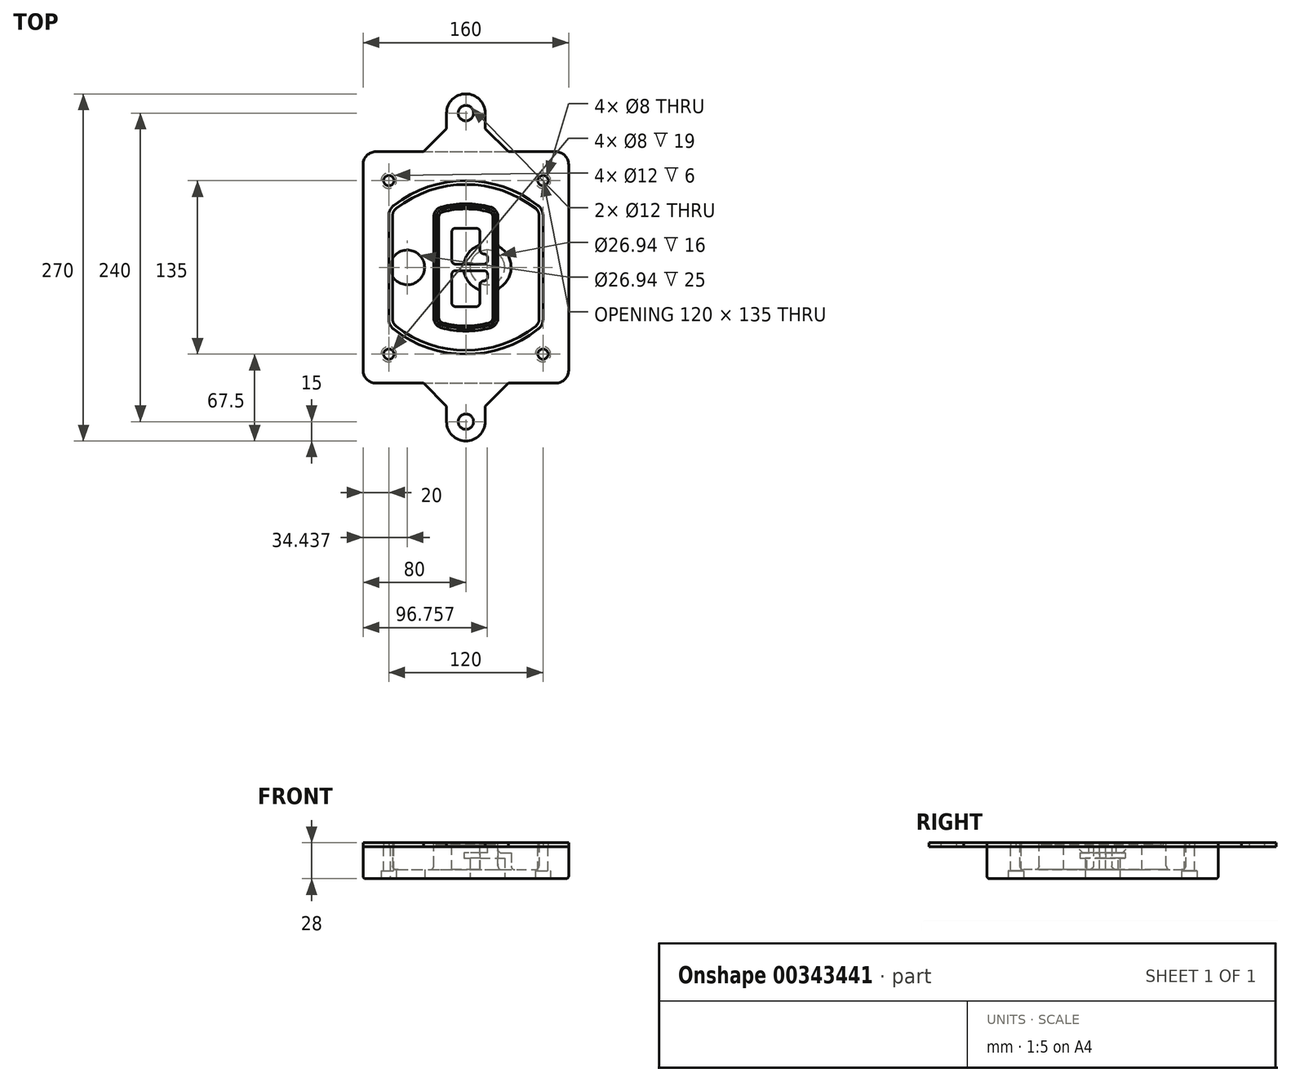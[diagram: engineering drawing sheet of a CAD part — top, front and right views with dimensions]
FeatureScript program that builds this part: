
annotation { "Feature Type Name" : "Feature", "Feature Type Description" : "" }
export const myFeature = defineFeature(function(context is Context, id is Id, definition is map)
    precondition{}
    {
        {
            var Q0;
            Q0=qCreatedBy(makeId("Top.planeOp"),FACE);
            var sketch = newSketch(context, id + "F0", { "sketchPlane" : qUnion([Q0])});
            skPoint(sketch, "E0.rect.middle", {"position": v(0, 0) * mm});
            skLineSegment(sketch, "E1.bottom", {"start": v(-70, -90) * mm, "end": v(70, -90) * mm});
            skLineSegment(sketch, "E1.top", {"start": v(-70, 90) * mm, "end": v(70, 90) * mm});
            skLineSegment(sketch, "E1.left", {"start": v(-80, -80) * mm, "end": v(-80, 80) * mm});
            skLineSegment(sketch, "E1.right", {"start": v(80, -80) * mm, "end": v(80, 80) * mm});
            skLineSegment(sketch, "E2", {"start": v(-80, 90) * mm, "end": v(80, -90) * mm, "construction": true});
            skLineSegment(sketch, "E3", {"start": v(80, 90) * mm, "end": v(-80, -90) * mm, "construction": true});
            skCircle(sketch, "E4", {"center": v(-60, 67.5) * mm, "radius": 4 * mm});
            skCircle(sketch, "E5", {"center": v(60, 67.5) * mm, "radius": 4 * mm});
            skCircle(sketch, "E6", {"center": v(60, -67.5) * mm, "radius": 4 * mm});
            skCircle(sketch, "E7", {"center": v(-60, -67.5) * mm, "radius": 4 * mm});
            skLineSegment(sketch, "E8", {"start": v(-60, 67.5) * mm, "end": v(60, 67.5) * mm, "construction": true});
            skLineSegment(sketch, "E9", {"start": v(60, 67.5) * mm, "end": v(60, -67.5) * mm, "construction": true});
            skLineSegment(sketch, "E10", {"start": v(60, -67.5) * mm, "end": v(-60, -67.5) * mm, "construction": true});
            skLineSegment(sketch, "E11", {"start": v(-60, -67.5) * mm, "end": v(-60, 67.5) * mm, "construction": true});
            skLineSegment(sketch, "E12", {"start": v(-60, 40.3) * mm, "end": v(-60, -40.3) * mm});
            skLineSegment(sketch, "E13", {"start": v(60, 40.3) * mm, "end": v(60, -40.3) * mm});
            skArc(sketch, "E14", {"start": v(56.15, 48.18) * mm, "mid": v(0, 67.5) * mm, "end": v(-56.15, 48.18) * mm});
            skArc(sketch, "E15", {"start": v(-56.15, -48.18) * mm, "mid": v(0, -67.5) * mm, "end": v(56.15, -48.18) * mm});
            skLineSegment(sketch, "E16", {"start": v(-60, 0) * mm, "end": v(60, 0) * mm, "construction": true});
            skPoint(sketch, "E17.visualSharp", {"position": v(-60, -45) * mm});
            skArc(sketch, "E17.filletArc", {"start": v(-60, -40.3) * mm, "mid": v(-58.99, -44.68) * mm, "end": v(-56.15, -48.18) * mm});
            skPoint(sketch, "E18.visualSharp", {"position": v(-60, 45) * mm});
            skArc(sketch, "E18.filletArc", {"start": v(-56.15, 48.18) * mm, "mid": v(-58.99, 44.68) * mm, "end": v(-60, 40.3) * mm});
            skPoint(sketch, "E19.visualSharp", {"position": v(60, 45) * mm});
            skArc(sketch, "E19.filletArc", {"start": v(60, 40.3) * mm, "mid": v(58.99, 44.68) * mm, "end": v(56.15, 48.18) * mm});
            skPoint(sketch, "E20.visualSharp", {"position": v(60, -45) * mm});
            skArc(sketch, "E20.filletArc", {"start": v(56.15, -48.18) * mm, "mid": v(58.99, -44.68) * mm, "end": v(60, -40.3) * mm});
            skPoint(sketch, "E21.visualSharp", {"position": v(-80, 90) * mm});
            skArc(sketch, "E21.filletArc", {"start": v(-70, 90) * mm, "mid": v(-77.07, 87.07) * mm, "end": v(-80, 80) * mm});
            skPoint(sketch, "E22.visualSharp", {"position": v(80, 90) * mm});
            skArc(sketch, "E22.filletArc", {"start": v(80, 80) * mm, "mid": v(77.07, 87.07) * mm, "end": v(70, 90) * mm});
            skPoint(sketch, "E23.visualSharp", {"position": v(80, -90) * mm});
            skArc(sketch, "E23.filletArc", {"start": v(70, -90) * mm, "mid": v(77.07, -87.07) * mm, "end": v(80, -80) * mm});
            skPoint(sketch, "E24.visualSharp", {"position": v(-80, -90) * mm});
            skArc(sketch, "E24.filletArc", {"start": v(-80, -80) * mm, "mid": v(-77.07, -87.07) * mm, "end": v(-70, -90) * mm});
            skArc(sketch, "E25.0", {"start": v(57, 40.3) * mm, "mid": v(56.3, 43.36) * mm, "end": v(54.3, 45.81) * mm});
            skLineSegment(sketch, "E25.1", {"start": v(57, 40.3) * mm, "end": v(57, -40.3) * mm});
            skArc(sketch, "E25.2", {"start": v(54.3, -45.81) * mm, "mid": v(56.3, -43.36) * mm, "end": v(57, -40.3) * mm});
            skArc(sketch, "E25.3", {"start": v(-54.3, -45.81) * mm, "mid": v(0, -64.5) * mm, "end": v(54.3, -45.81) * mm});
            skArc(sketch, "E25.4", {"start": v(-57, -40.3) * mm, "mid": v(-56.3, -43.36) * mm, "end": v(-54.3, -45.81) * mm});
            skArc(sketch, "E25.5", {"start": v(54.3, 45.81) * mm, "mid": v(0, 64.5) * mm, "end": v(-54.3, 45.81) * mm});
            skLineSegment(sketch, "E25.6", {"start": v(-57, 40.3) * mm, "end": v(-57, -40.3) * mm});
            skArc(sketch, "E25.7", {"start": v(-54.3, 45.81) * mm, "mid": v(-56.3, 43.36) * mm, "end": v(-57, 40.3) * mm});
            skArc(sketch, "E26.0", {"start": v(-58.62, 51.33) * mm, "mid": v(-62.58, 46.43) * mm, "end": v(-64, 40.3) * mm});
            skArc(sketch, "E26.1", {"start": v(58.62, 51.33) * mm, "mid": v(0, 71.5) * mm, "end": v(-58.62, 51.33) * mm});
            skArc(sketch, "E26.2", {"start": v(64, 40.3) * mm, "mid": v(62.58, 46.43) * mm, "end": v(58.62, 51.33) * mm});
            skLineSegment(sketch, "E26.3", {"start": v(64, 40.3) * mm, "end": v(64, -40.3) * mm});
            skArc(sketch, "E26.4", {"start": v(58.62, -51.33) * mm, "mid": v(62.58, -46.43) * mm, "end": v(64, -40.3) * mm});
            skLineSegment(sketch, "E26.5", {"start": v(-64, 40.3) * mm, "end": v(-64, -40.3) * mm});
            skArc(sketch, "E26.6", {"start": v(-58.62, -51.33) * mm, "mid": v(0, -71.5) * mm, "end": v(58.62, -51.33) * mm});
            skArc(sketch, "E26.7", {"start": v(-64, -40.3) * mm, "mid": v(-62.58, -46.43) * mm, "end": v(-58.62, -51.33) * mm});
            skSolve(sketch);
        }
        {
            var Q0;
            Q0=makeQuery(id+"F0.imprint","IMPRINT",FACE,{"disambiguationData":[TD([[makeQuery(id+"F0.imprint","IMPRINT",EDGE,{"derivedFrom":sQuery(id+"F0.wireOp",EDGE,"E1.bottom")}),1.0]])]});
            var Q1;
            Q1=makeQuery(id+"F0.imprint","IMPRINT",FACE,{"disambiguationData":[TD([[makeQuery(id+"F0.imprint","IMPRINT",EDGE,{"derivedFrom":sQuery(id+"F0.wireOp",EDGE,"E12")}),1.0]])]});
            var Q2;
            Q2=makeQuery(id+"F0.imprint","IMPRINT",FACE,{"disambiguationData":[TD([[makeQuery(id+"F0.imprint","IMPRINT",EDGE,{"derivedFrom":sQuery(id+"F0.wireOp",EDGE,"E25.0")}),1.0]])]});
            var Q3;
            Q3=makeQuery(id+"F0.imprint","IMPRINT",FACE,{"disambiguationData":[TD([[makeQuery(id+"F0.imprint","IMPRINT",EDGE,{"derivedFrom":sQuery(id+"F0.wireOp",EDGE,"E12")}),-1.0]])]});
            extrude(context, id + "F1", {"entities" : qUnion([Q0, Q1, Q2, Q3]), "oppositeDirection" : true, "depth" : 25 * mm});
        }
        {
            var Q0;
            Q0=makeQuery(id+"F0.imprint","IMPRINT",FACE,{"disambiguationData":[TD([[makeQuery(id+"F0.imprint","IMPRINT",EDGE,{"derivedFrom":sQuery(id+"F0.wireOp",EDGE,"E12")}),1.0]])]});
            extrude(context, id + "F2", {"entities" : qUnion([Q0]), "operationType" : NewBodyOperationType.ADD, "depth" : 3 * mm});
        }
        {
            var Q0;
            Q0=makeQuery(id+"F0.imprint","IMPRINT",FACE,{"disambiguationData":[TD([[makeQuery(id+"F0.imprint","IMPRINT",EDGE,{"derivedFrom":sQuery(id+"F0.wireOp",EDGE,"E25.0")}),1.0]])]});
            extrude(context, id + "F3", {"entities" : qUnion([Q0]), "operationType" : NewBodyOperationType.REMOVE, "oppositeDirection" : true, "depth" : 18 * mm});
        }
        {
            var Q0;
            Q0=makeQuery(id+"F2.opExtrude","CAP_FACE",FACE,{"disambiguationData":[OSD([sQuery(id+"F0.wireOp",EDGE,"E12"),sQuery(id+"F0.wireOp",EDGE,"E13"),sQuery(id+"F0.wireOp",EDGE,"E14"),sQuery(id+"F0.wireOp",EDGE,"E15"),sQuery(id+"F0.wireOp",EDGE,"E17.filletArc"),sQuery(id+"F0.wireOp",EDGE,"E18.filletArc"),sQuery(id+"F0.wireOp",EDGE,"E19.filletArc"),sQuery(id+"F0.wireOp",EDGE,"E20.filletArc"),sQuery(id+"F0.wireOp",EDGE,"E25.0"),sQuery(id+"F0.wireOp",EDGE,"E25.1"),sQuery(id+"F0.wireOp",EDGE,"E25.2"),sQuery(id+"F0.wireOp",EDGE,"E25.3"),sQuery(id+"F0.wireOp",EDGE,"E25.4"),sQuery(id+"F0.wireOp",EDGE,"E25.5"),sQuery(id+"F0.wireOp",EDGE,"E25.6"),sQuery(id+"F0.wireOp",EDGE,"E25.7")])],"isStart":false});
            var sketch = newSketch(context, id + "F4", { "sketchPlane" : qUnion([Q0])});
            skArc(sketch, "E27.0", {"start": v(-19.08, -46.97) * mm, "mid": v(0, -49.5) * mm, "end": v(19.08, -46.97) * mm});
            skArc(sketch, "E28.0", {"start": v(19.08, 46.97) * mm, "mid": v(0, 49.5) * mm, "end": v(-19.08, 46.97) * mm});
            skLineSegment(sketch, "E29", {"start": v(-25, 39.25) * mm, "end": v(-25, -39.25) * mm});
            skLineSegment(sketch, "E30", {"start": v(25, 39.25) * mm, "end": v(25, -39.25) * mm});
            skLineSegment(sketch, "E31", {"start": v(-25, 45.1) * mm, "end": v(25, 45.1) * mm, "construction": true});
            skLineSegment(sketch, "E32", {"start": v(-25, -45.1) * mm, "end": v(25, -45.1) * mm, "construction": true});
            skPoint(sketch, "E33.visualSharp", {"position": v(-25, 45.1) * mm});
            skArc(sketch, "E33.filletArc", {"start": v(-19.08, 46.97) * mm, "mid": v(-23.35, 44.11) * mm, "end": v(-25, 39.25) * mm});
            skPoint(sketch, "E34.visualSharp", {"position": v(25, 45.1) * mm});
            skArc(sketch, "E34.filletArc", {"start": v(25, 39.25) * mm, "mid": v(23.35, 44.11) * mm, "end": v(19.08, 46.97) * mm});
            skPoint(sketch, "E35.visualSharp", {"position": v(25, -45.1) * mm});
            skArc(sketch, "E35.filletArc", {"start": v(19.08, -46.97) * mm, "mid": v(23.35, -44.11) * mm, "end": v(25, -39.25) * mm});
            skPoint(sketch, "E36.visualSharp", {"position": v(-25, -45.1) * mm});
            skArc(sketch, "E36.filletArc", {"start": v(-25, -39.25) * mm, "mid": v(-23.35, -44.11) * mm, "end": v(-19.08, -46.97) * mm});
            skArc(sketch, "E37.0", {"start": v(54.3, 45.81) * mm, "mid": v(0, 64.5) * mm, "end": v(-54.3, 45.81) * mm});
            skArc(sketch, "E37.1", {"start": v(-54.3, 45.81) * mm, "mid": v(-56.3, 43.36) * mm, "end": v(-57, 40.3) * mm});
            skLineSegment(sketch, "E37.2", {"start": v(-57, 40.3) * mm, "end": v(-57, -40.3) * mm});
            skArc(sketch, "E37.3", {"start": v(-57, -40.3) * mm, "mid": v(-56.3, -43.36) * mm, "end": v(-54.3, -45.81) * mm});
            skArc(sketch, "E37.4", {"start": v(-54.3, -45.81) * mm, "mid": v(0, -64.5) * mm, "end": v(54.3, -45.81) * mm});
            skArc(sketch, "E37.5", {"start": v(54.3, -45.81) * mm, "mid": v(56.3, -43.36) * mm, "end": v(57, -40.3) * mm});
            skLineSegment(sketch, "E37.6", {"start": v(57, 40.3) * mm, "end": v(57, -40.3) * mm});
            skArc(sketch, "E37.7", {"start": v(57, 40.3) * mm, "mid": v(56.3, 43.36) * mm, "end": v(54.3, 45.81) * mm});
            skLineSegment(sketch, "E38.0", {"start": v(23, 39.25) * mm, "end": v(23, -39.25) * mm});
            skArc(sketch, "E38.1", {"start": v(18.56, -45.04) * mm, "mid": v(21.76, -42.9) * mm, "end": v(23, -39.25) * mm});
            skArc(sketch, "E38.2", {"start": v(-18.56, -45.04) * mm, "mid": v(0, -47.5) * mm, "end": v(18.56, -45.04) * mm});
            skArc(sketch, "E38.3", {"start": v(-23, -39.25) * mm, "mid": v(-21.76, -42.9) * mm, "end": v(-18.56, -45.04) * mm});
            skLineSegment(sketch, "E38.4", {"start": v(-23, 39.25) * mm, "end": v(-23, -39.25) * mm});
            skArc(sketch, "E38.5", {"start": v(23, 39.25) * mm, "mid": v(21.76, 42.9) * mm, "end": v(18.56, 45.04) * mm});
            skArc(sketch, "E38.6", {"start": v(-18.56, 45.04) * mm, "mid": v(-21.76, 42.9) * mm, "end": v(-23, 39.25) * mm});
            skArc(sketch, "E38.7", {"start": v(18.56, 45.04) * mm, "mid": v(0, 47.5) * mm, "end": v(-18.56, 45.04) * mm});
            skArc(sketch, "E39.0", {"start": v(21, 39.25) * mm, "mid": v(20.18, 41.68) * mm, "end": v(18.04, 43.1) * mm});
            skLineSegment(sketch, "E39.1", {"start": v(21, 39.25) * mm, "end": v(21, -39.25) * mm});
            skArc(sketch, "E39.2", {"start": v(18.04, -43.1) * mm, "mid": v(20.18, -41.68) * mm, "end": v(21, -39.25) * mm});
            skArc(sketch, "E39.3", {"start": v(-18.04, -43.1) * mm, "mid": v(0, -45.5) * mm, "end": v(18.04, -43.1) * mm});
            skArc(sketch, "E39.4", {"start": v(-21, -39.25) * mm, "mid": v(-20.18, -41.68) * mm, "end": v(-18.04, -43.1) * mm});
            skArc(sketch, "E39.5", {"start": v(18.04, 43.1) * mm, "mid": v(0, 45.5) * mm, "end": v(-18.04, 43.1) * mm});
            skLineSegment(sketch, "E39.6", {"start": v(-21, 39.25) * mm, "end": v(-21, -39.25) * mm});
            skArc(sketch, "E39.7", {"start": v(-18.04, 43.1) * mm, "mid": v(-20.18, 41.68) * mm, "end": v(-21, 39.25) * mm});
            skLineSegment(sketch, "E40", {"start": v(-25, 0) * mm, "end": v(25, 0) * mm, "construction": true});
            skLineSegment(sketch, "E41", {"start": v(-11, 5.5) * mm, "end": v(-11, 27.5) * mm});
            skLineSegment(sketch, "E42", {"start": v(-8, 30.5) * mm, "end": v(8, 30.5) * mm});
            skLineSegment(sketch, "E43", {"start": v(11, 27.5) * mm, "end": v(11, 13.5) * mm});
            skLineSegment(sketch, "E44", {"start": v(14, 10.5) * mm, "end": v(14, 10.5) * mm});
            skLineSegment(sketch, "E45", {"start": v(17, 7.5) * mm, "end": v(17, 5.5) * mm});
            skLineSegment(sketch, "E46", {"start": v(14, 2.5) * mm, "end": v(-8, 2.5) * mm});
            skPoint(sketch, "E47.visualSharp", {"position": v(-11, 30.5) * mm});
            skArc(sketch, "E47.filletArc", {"start": v(-8, 30.5) * mm, "mid": v(-10.12, 29.62) * mm, "end": v(-11, 27.5) * mm});
            skPoint(sketch, "E48.visualSharp", {"position": v(11, 30.5) * mm});
            skArc(sketch, "E48.filletArc", {"start": v(11, 27.5) * mm, "mid": v(10.12, 29.62) * mm, "end": v(8, 30.5) * mm});
            skPoint(sketch, "E49.visualSharp", {"position": v(11, 10.5) * mm});
            skArc(sketch, "E49.filletArc", {"start": v(11, 13.5) * mm, "mid": v(11.88, 11.38) * mm, "end": v(14, 10.5) * mm});
            skPoint(sketch, "E50.visualSharp", {"position": v(17, 10.5) * mm});
            skArc(sketch, "E50.filletArc", {"start": v(17, 7.5) * mm, "mid": v(16.12, 9.62) * mm, "end": v(14, 10.5) * mm});
            skPoint(sketch, "E51.visualSharp", {"position": v(17, 2.5) * mm});
            skArc(sketch, "E51.filletArc", {"start": v(14, 2.5) * mm, "mid": v(16.12, 3.38) * mm, "end": v(17, 5.5) * mm});
            skPoint(sketch, "E52.visualSharp", {"position": v(-11, 2.5) * mm});
            skArc(sketch, "E52.filletArc", {"start": v(-11, 5.5) * mm, "mid": v(-10.12, 3.38) * mm, "end": v(-8, 2.5) * mm});
            skLineSegment(sketch, "E53.0.MirrorCS", {"start": v(14, -2.5) * mm, "end": v(-8, -2.5) * mm});
            skArc(sketch, "E54.0.MirrorCS", {"start": v(-11, -5.5) * mm, "mid": v(-10.12, -3.38) * mm, "end": v(-8, -2.5) * mm});
            skLineSegment(sketch, "E55.0.MirrorCS", {"start": v(-11, -5.5) * mm, "end": v(-11, -27.5) * mm});
            skArc(sketch, "E56.0.MirrorCS", {"start": v(-8, -30.5) * mm, "mid": v(-10.12, -29.62) * mm, "end": v(-11, -27.5) * mm});
            skLineSegment(sketch, "E57.0.MirrorCS", {"start": v(-8, -30.5) * mm, "end": v(8, -30.5) * mm});
            skArc(sketch, "E58.0.MirrorCS", {"start": v(11, -27.5) * mm, "mid": v(10.12, -29.62) * mm, "end": v(8, -30.5) * mm});
            skLineSegment(sketch, "E59.0.MirrorCS", {"start": v(11, -27.5) * mm, "end": v(11, -13.5) * mm});
            skArc(sketch, "E60.0.MirrorCS", {"start": v(11, -13.5) * mm, "mid": v(11.88, -11.38) * mm, "end": v(14, -10.5) * mm});
            skArc(sketch, "E61.0.MirrorCS", {"start": v(17, -7.5) * mm, "mid": v(16.12, -9.62) * mm, "end": v(14, -10.5) * mm});
            skLineSegment(sketch, "E62.0.MirrorCS", {"start": v(17, -7.5) * mm, "end": v(17, -5.5) * mm});
            skArc(sketch, "E63.0.MirrorCS", {"start": v(14, -2.5) * mm, "mid": v(16.12, -3.38) * mm, "end": v(17, -5.5) * mm});
            skSolve(sketch);
        }
        {
            var Q0;
            Q0=makeQuery(id+"F4.imprint","IMPRINT",FACE,{"disambiguationData":[TD([[makeQuery(id+"F4.imprint","IMPRINT",EDGE,{"derivedFrom":sQuery(id+"F4.wireOp",EDGE,"E27.0")}),1.0]])]});
            var Q1;
            Q1=makeQuery(id+"F4.imprint","IMPRINT",FACE,{"disambiguationData":[TD([[makeQuery(id+"F4.imprint","IMPRINT",EDGE,{"derivedFrom":sQuery(id+"F4.wireOp",EDGE,"E38.0")}),-1.0]])]});
            var Q2;
            Q2=makeQuery(id+"F4.imprint","IMPRINT",FACE,{"disambiguationData":[TD([[makeQuery(id+"F4.imprint","IMPRINT",EDGE,{"derivedFrom":sQuery(id+"F4.wireOp",EDGE,"E39.0")}),1.0]])]});
            extrude(context, id + "F5", {"entities" : qUnion([Q0, Q1, Q2]), "operationType" : NewBodyOperationType.ADD, "endBound" : BoundingType.UP_TO_NEXT, "oppositeDirection" : true, "depth" : 25 * mm});
        }
        {
            var Q0;
            Q0=makeQuery(id+"F4.imprint","IMPRINT",FACE,{"disambiguationData":[TD([[makeQuery(id+"F4.imprint","IMPRINT",EDGE,{"derivedFrom":sQuery(id+"F4.wireOp",EDGE,"E38.0")}),-1.0]])]});
            extrude(context, id + "F6", {"entities" : qUnion([Q0]), "operationType" : NewBodyOperationType.REMOVE, "oppositeDirection" : true, "depth" : 2 * mm});
        }
        {
            var Q0;
            Q0=makeQuery(id+"F1.opExtrude","CAP_FACE",FACE,{"disambiguationData":[OSD([sQuery(id+"F0.wireOp",EDGE,"E1.bottom"),sQuery(id+"F0.wireOp",EDGE,"E1.top"),sQuery(id+"F0.wireOp",EDGE,"E1.left"),sQuery(id+"F0.wireOp",EDGE,"E1.right"),sQuery(id+"F0.wireOp",EDGE,"E4"),sQuery(id+"F0.wireOp",EDGE,"E5"),sQuery(id+"F0.wireOp",EDGE,"E6"),sQuery(id+"F0.wireOp",EDGE,"E7"),sQuery(id+"F0.wireOp",EDGE,"E21.filletArc"),sQuery(id+"F0.wireOp",EDGE,"E22.filletArc"),sQuery(id+"F0.wireOp",EDGE,"E23.filletArc"),sQuery(id+"F0.wireOp",EDGE,"E24.filletArc")])],"isStart":false});
            var sketch = newSketch(context, id + "F7", { "sketchPlane" : qUnion([Q0])});
            skCircle(sketch, "E64", {"center": v(16.76, 0) * mm, "radius": 13.47 * mm});
            skCircle(sketch, "E65", {"center": v(-45.56, 0) * mm, "radius": 13.47 * mm});
            skLineSegment(sketch, "E66", {"start": v(80, 0) * mm, "end": v(-80, 0) * mm});
            skCircle(sketch, "E67", {"center": v(16.76, 0) * mm, "radius": 18.47 * mm});
            skCircle(sketch, "E68", {"center": v(60, -67.5) * mm, "radius": 6 * mm});
            skCircle(sketch, "E69", {"center": v(-60, -67.5) * mm, "radius": 6 * mm});
            skCircle(sketch, "E70", {"center": v(-60, 67.5) * mm, "radius": 6 * mm});
            skCircle(sketch, "E71", {"center": v(60, 67.5) * mm, "radius": 6 * mm});
            skSolve(sketch);
        }
        {
            var Q0;
            {var subQ1=sQuery(id+"F7.wireOp",EDGE,"E66");var subQ4=sQuery(id+"F7.wireOp",EDGE,"E64");var subQ6=makeQuery(id+"F7.imprint","INTERSECT",VERTEX,{"disambiguationData":[OD(0.0)],"derivedFrom":[subQ4,subQ1]});Q0=makeQuery(id+"F7.imprint","IMPRINT",FACE,{"disambiguationData":[TD([[makeQuery(id+"F7.imprint","IMPRINT",EDGE,{"disambiguationData":[TD([[subQ6,-1.0]])],"derivedFrom":subQ4}),-1.0]])]});}
            var Q1;
            {var subQ0=sQuery(id+"F7.wireOp",EDGE,"E66");var subQ1=sQuery(id+"F7.wireOp",EDGE,"E64");var subQ3=makeQuery(id+"F7.imprint","INTERSECT",VERTEX,{"disambiguationData":[OD(0.0)],"derivedFrom":[subQ1,subQ0]});Q1=makeQuery(id+"F7.imprint","IMPRINT",FACE,{"disambiguationData":[TD([[makeQuery(id+"F7.imprint","IMPRINT",EDGE,{"disambiguationData":[TD([[subQ3,-1.0]])],"derivedFrom":subQ1}),1.0]])]});}
            var Q2;
            {var subQ0=sQuery(id+"F7.wireOp",EDGE,"E66");var subQ1=sQuery(id+"F7.wireOp",EDGE,"E64");var subQ3=makeQuery(id+"F7.imprint","INTERSECT",VERTEX,{"disambiguationData":[OD(0.0)],"derivedFrom":[subQ1,subQ0]});Q2=makeQuery(id+"F7.imprint","IMPRINT",FACE,{"disambiguationData":[TD([[makeQuery(id+"F7.imprint","IMPRINT",EDGE,{"disambiguationData":[TD([[subQ3,1.0]])],"derivedFrom":subQ1}),1.0]])]});}
            var Q3;
            {var subQ1=sQuery(id+"F7.wireOp",EDGE,"E66");var subQ4=sQuery(id+"F7.wireOp",EDGE,"E64");var subQ6=makeQuery(id+"F7.imprint","INTERSECT",VERTEX,{"disambiguationData":[OD(0.0)],"derivedFrom":[subQ4,subQ1]});Q3=makeQuery(id+"F7.imprint","IMPRINT",FACE,{"disambiguationData":[TD([[makeQuery(id+"F7.imprint","IMPRINT",EDGE,{"disambiguationData":[TD([[subQ6,1.0]])],"derivedFrom":subQ4}),-1.0]])]});}
            extrude(context, id + "F8", {"entities" : qUnion([Q0, Q1, Q2, Q3]), "operationType" : NewBodyOperationType.ADD, "oppositeDirection" : true, "depth" : 20 * mm});
        }
        {
            var Q0;
            {var subQ0=sQuery(id+"F7.wireOp",EDGE,"E66");var subQ1=sQuery(id+"F7.wireOp",EDGE,"E64");var subQ3=makeQuery(id+"F7.imprint","INTERSECT",VERTEX,{"disambiguationData":[OD(0.0)],"derivedFrom":[subQ1,subQ0]});Q0=makeQuery(id+"F7.imprint","IMPRINT",FACE,{"disambiguationData":[TD([[makeQuery(id+"F7.imprint","IMPRINT",EDGE,{"disambiguationData":[TD([[subQ3,-1.0]])],"derivedFrom":subQ1}),1.0]])]});}
            var Q1;
            {var subQ0=sQuery(id+"F7.wireOp",EDGE,"E66");var subQ1=sQuery(id+"F7.wireOp",EDGE,"E64");var subQ3=makeQuery(id+"F7.imprint","INTERSECT",VERTEX,{"disambiguationData":[OD(0.0)],"derivedFrom":[subQ1,subQ0]});Q1=makeQuery(id+"F7.imprint","IMPRINT",FACE,{"disambiguationData":[TD([[makeQuery(id+"F7.imprint","IMPRINT",EDGE,{"disambiguationData":[TD([[subQ3,1.0]])],"derivedFrom":subQ1}),1.0]])]});}
            extrude(context, id + "F9", {"entities" : qUnion([Q0, Q1]), "operationType" : NewBodyOperationType.REMOVE, "oppositeDirection" : true, "depth" : 16 * mm});
        }
        {
            var Q0;
            {var subQ0=sQuery(id+"F7.wireOp",EDGE,"E66");var subQ1=sQuery(id+"F7.wireOp",EDGE,"E65");var subQ3=makeQuery(id+"F7.imprint","INTERSECT",VERTEX,{"disambiguationData":[OD(0.0)],"derivedFrom":[subQ1,subQ0]});Q0=makeQuery(id+"F7.imprint","IMPRINT",FACE,{"disambiguationData":[TD([[makeQuery(id+"F7.imprint","IMPRINT",EDGE,{"disambiguationData":[TD([[subQ3,-1.0]])],"derivedFrom":subQ1}),1.0]])]});}
            var Q1;
            {var subQ0=sQuery(id+"F7.wireOp",EDGE,"E66");var subQ1=sQuery(id+"F7.wireOp",EDGE,"E65");var subQ3=makeQuery(id+"F7.imprint","INTERSECT",VERTEX,{"disambiguationData":[OD(0.0)],"derivedFrom":[subQ1,subQ0]});Q1=makeQuery(id+"F7.imprint","IMPRINT",FACE,{"disambiguationData":[TD([[makeQuery(id+"F7.imprint","IMPRINT",EDGE,{"disambiguationData":[TD([[subQ3,1.0]])],"derivedFrom":subQ1}),1.0]])]});}
            extrude(context, id + "F10", {"entities" : qUnion([Q0, Q1]), "operationType" : NewBodyOperationType.REMOVE, "oppositeDirection" : true, "depth" : 25 * mm});
        }
        {
            var Q0;
            Q0=makeQuery(id+"F7.imprint","IMPRINT",FACE,{"disambiguationData":[TD([[makeQuery(id+"F7.imprint","IMPRINT",EDGE,{"derivedFrom":sQuery(id+"F7.wireOp",EDGE,"E68")}),1.0]])]});
            var Q1;
            Q1=makeQuery(id+"F7.imprint","IMPRINT",FACE,{"disambiguationData":[TD([[makeQuery(id+"F7.imprint","IMPRINT",EDGE,{"derivedFrom":makeQuery(id+"F1.opExtrude","CAP_EDGE",EDGE,{"disambiguationData":[OSD([sQuery(id+"F0.wireOp",EDGE,"E5")])],"isStart":false})}),-1.0]])]});
            var Q2;
            Q2=makeQuery(id+"F7.imprint","IMPRINT",FACE,{"disambiguationData":[TD([[makeQuery(id+"F7.imprint","IMPRINT",EDGE,{"derivedFrom":sQuery(id+"F7.wireOp",EDGE,"E69")}),1.0]])]});
            var Q3;
            Q3=makeQuery(id+"F7.imprint","IMPRINT",FACE,{"disambiguationData":[TD([[makeQuery(id+"F7.imprint","IMPRINT",EDGE,{"derivedFrom":makeQuery(id+"F1.opExtrude","CAP_EDGE",EDGE,{"disambiguationData":[OSD([sQuery(id+"F0.wireOp",EDGE,"E4")])],"isStart":false})}),-1.0]])]});
            var Q4;
            Q4=makeQuery(id+"F7.imprint","IMPRINT",FACE,{"disambiguationData":[TD([[makeQuery(id+"F7.imprint","IMPRINT",EDGE,{"derivedFrom":sQuery(id+"F7.wireOp",EDGE,"E70")}),1.0]])]});
            var Q5;
            Q5=makeQuery(id+"F7.imprint","IMPRINT",FACE,{"disambiguationData":[TD([[makeQuery(id+"F7.imprint","IMPRINT",EDGE,{"derivedFrom":makeQuery(id+"F1.opExtrude","CAP_EDGE",EDGE,{"disambiguationData":[OSD([sQuery(id+"F0.wireOp",EDGE,"E7")])],"isStart":false})}),-1.0]])]});
            var Q6;
            Q6=makeQuery(id+"F7.imprint","IMPRINT",FACE,{"disambiguationData":[TD([[makeQuery(id+"F7.imprint","IMPRINT",EDGE,{"derivedFrom":sQuery(id+"F7.wireOp",EDGE,"E71")}),1.0]])]});
            var Q7;
            Q7=makeQuery(id+"F7.imprint","IMPRINT",FACE,{"disambiguationData":[TD([[makeQuery(id+"F7.imprint","IMPRINT",EDGE,{"derivedFrom":makeQuery(id+"F1.opExtrude","CAP_EDGE",EDGE,{"disambiguationData":[OSD([sQuery(id+"F0.wireOp",EDGE,"E6")])],"isStart":false})}),-1.0]])]});
            extrude(context, id + "F11", {"entities" : qUnion([Q0, Q1, Q2, Q3, Q4, Q5, Q6, Q7]), "operationType" : NewBodyOperationType.REMOVE, "oppositeDirection" : true, "depth" : 6 * mm});
        }
        {
            var Q0;
            Q0=makeQuery(id+"F9.boolean.opBoolean","COPY",FACE,{"derivedFrom":makeQuery(id+"F9.opExtrude","CAP_FACE",FACE,{"disambiguationData":[OSD([sQuery(id+"F7.wireOp",EDGE,"E64")])],"isStart":false})});
            var sketch = newSketch(context, id + "F12", { "sketchPlane" : qUnion([Q0])});
            skArc(sketch, "E72.0", {"start": v(11, 17.55) * mm, "mid": v(2.57, 11.82) * mm, "end": v(-1.54, 2.5) * mm});
            skArc(sketch, "E72.1", {"start": v(-1.54, -2.5) * mm, "mid": v(2.57, -11.82) * mm, "end": v(11, -17.55) * mm});
            skLineSegment(sketch, "E73", {"start": v(-1.54, -2.5) * mm, "end": v(14, -2.5) * mm});
            skLineSegment(sketch, "E74.0", {"start": v(14, 2.5) * mm, "end": v(-1.54, 2.5) * mm});
            skArc(sketch, "E74.1", {"start": v(14, 2.5) * mm, "mid": v(16.12, 3.38) * mm, "end": v(17, 5.5) * mm});
            skLineSegment(sketch, "E74.2", {"start": v(17, 7.5) * mm, "end": v(17, 5.5) * mm});
            skArc(sketch, "E74.3", {"start": v(17, 7.5) * mm, "mid": v(16.12, 9.62) * mm, "end": v(14, 10.5) * mm});
            skArc(sketch, "E74.4", {"start": v(11, 13.5) * mm, "mid": v(11.88, 11.38) * mm, "end": v(14, 10.5) * mm});
            skLineSegment(sketch, "E74.5", {"start": v(11, 17.55) * mm, "end": v(11, 13.5) * mm});
            skLineSegment(sketch, "E74.7", {"start": v(14, -2.5) * mm, "end": v(-1.54, -2.5) * mm});
            skArc(sketch, "E74.8", {"start": v(14, -2.5) * mm, "mid": v(16.12, -3.38) * mm, "end": v(17, -5.5) * mm});
            skLineSegment(sketch, "E74.9", {"start": v(17, -7.5) * mm, "end": v(17, -5.5) * mm});
            skArc(sketch, "E74.10", {"start": v(17, -7.5) * mm, "mid": v(16.12, -9.62) * mm, "end": v(14, -10.5) * mm});
            skArc(sketch, "E74.11", {"start": v(11, -13.5) * mm, "mid": v(11.88, -11.38) * mm, "end": v(14, -10.5) * mm});
            skLineSegment(sketch, "E74.12", {"start": v(11, -17.55) * mm, "end": v(11, -13.5) * mm});
            skPoint(sketch, "E75.orphan", {"position": v(11, -27.5) * mm});
            skPoint(sketch, "E76.orphan", {"position": v(-8, -2.5) * mm});
            skPoint(sketch, "E77.orphan", {"position": v(-8, 2.5) * mm});
            skPoint(sketch, "E78.orphan", {"position": v(11, 27.5) * mm});
            skSolve(sketch);
        }
        {
            var Q0;
            {var subQ7=sQuery(id+"F12.wireOp",EDGE,"E72.0");var subQ14=sQuery(id+"F12.wireOp",EDGE,"E72.1");var subQ16=sQuery(id+"F12.wireOp",EDGE,"E74.1");var subQ18=sQuery(id+"F12.wireOp",EDGE,"E74.8");Q0=qUnion([makeQuery(id+"F12.imprint","IMPRINT",FACE,{"disambiguationData":[TD([[makeQuery(id+"F12.imprint","IMPRINT",EDGE,{"derivedFrom":subQ7}),1.0]])]}),makeQuery(id+"F12.imprint","IMPRINT",FACE,{"disambiguationData":[TD([[makeQuery(id+"F12.imprint","IMPRINT",EDGE,{"derivedFrom":subQ14}),1.0]])]}),makeQuery(id+"F12.imprint","IMPRINT",FACE,{"disambiguationData":[TD([[makeQuery(id+"F12.imprint","IMPRINT",EDGE,{"derivedFrom":subQ16}),1.0]])]}),makeQuery(id+"F12.imprint","IMPRINT",FACE,{"disambiguationData":[TD([[makeQuery(id+"F12.imprint","IMPRINT",EDGE,{"derivedFrom":subQ18}),-1.0]])]})]);}
            var Q1;
            Q1=makeQuery(id+"F5.boolean.opBoolean","SPLIT",FACE,{"disambiguationData":[TD([makeQuery(id+"F5.opExtrude","SWEPT_FACE",FACE,{"disambiguationData":[OSD([sQuery(id+"F4.wireOp",EDGE,"E41")])]})])],"derivedFrom":makeQuery(id+"F3.boolean.opBoolean","COPY",FACE,{"derivedFrom":makeQuery(id+"F3.opExtrude","CAP_FACE",FACE,{"disambiguationData":[OSD([sQuery(id+"F0.wireOp",EDGE,"E25.0"),sQuery(id+"F0.wireOp",EDGE,"E25.1"),sQuery(id+"F0.wireOp",EDGE,"E25.2"),sQuery(id+"F0.wireOp",EDGE,"E25.3"),sQuery(id+"F0.wireOp",EDGE,"E25.4"),sQuery(id+"F0.wireOp",EDGE,"E25.5"),sQuery(id+"F0.wireOp",EDGE,"E25.6"),sQuery(id+"F0.wireOp",EDGE,"E25.7")])],"isStart":false})})});
            extrude(context, id + "F13", {"entities" : qUnion([Q0]), "operationType" : NewBodyOperationType.REMOVE, "endBound" : BoundingType.UP_TO_SURFACE, "endBoundEntityFace" : qUnion([Q1]), "depth" : 25 * mm});
        }
        {
            var Q0;
            Q0=makeQuery(id+"F3.boolean.opBoolean","COPY",EDGE,{"derivedFrom":makeQuery(id+"F3.opExtrude","CAP_EDGE",EDGE,{"disambiguationData":[OSD([sQuery(id+"F0.wireOp",EDGE,"E25.6")])],"isStart":false})});
            var Q1;
            Q1=makeQuery(id+"F8.boolean.opBoolean","INTERSECT",EDGE,{"derivedFrom":[makeQuery(id+"F5.opExtrude","SWEPT_FACE",FACE,{"disambiguationData":[OSD([sQuery(id+"F4.wireOp",EDGE,"E30")])]}),makeQuery(id+"F8.opExtrude","CAP_FACE",FACE,{"disambiguationData":[OSD([sQuery(id+"F7.wireOp",EDGE,"E67")])],"isStart":false})]});
            var Q2;
            Q2=makeQuery(id+"F8.boolean.opBoolean","INTERSECT",EDGE,{"disambiguationData":[OD(1.0)],"derivedFrom":[makeQuery(id+"F5.opExtrude","SWEPT_FACE",FACE,{"disambiguationData":[OSD([sQuery(id+"F4.wireOp",EDGE,"E30")])]}),makeQuery(id+"F8.opExtrude","SWEPT_FACE",FACE,{"disambiguationData":[OSD([sQuery(id+"F7.wireOp",EDGE,"E67")])]})]});
            var Q3;
            {var subQ0=sQuery(id+"F4.wireOp",EDGE,"E30");Q3=makeQuery(id+"F8.boolean.opBoolean","SPLIT",EDGE,{"disambiguationData":[TD([makeQuery(id+"F5.opExtrude","SWEPT_FACE",FACE,{"disambiguationData":[OSD([sQuery(id+"F4.wireOp",EDGE,"E35.filletArc")])]})])],"derivedFrom":makeQuery(id+"F5.opExtrude","CAP_EDGE",EDGE,{"disambiguationData":[OSD([subQ0])],"isStart":false})});}
            var Q4;
            {var subQ0=sQuery(id+"F0.wireOp",EDGE,"E25.7");var subQ1=sQuery(id+"F0.wireOp",EDGE,"E25.1");var subQ2=sQuery(id+"F0.wireOp",EDGE,"E25.6");var subQ3=sQuery(id+"F0.wireOp",EDGE,"E25.5");var subQ4=sQuery(id+"F0.wireOp",EDGE,"E25.4");var subQ5=sQuery(id+"F0.wireOp",EDGE,"E25.0");var subQ6=sQuery(id+"F0.wireOp",EDGE,"E25.2");var subQ7=sQuery(id+"F0.wireOp",EDGE,"E25.3");Q4=makeQuery(id+"F8.boolean.opBoolean","INTERSECT",EDGE,{"derivedFrom":[makeQuery(id+"F5.boolean.opBoolean","SPLIT",FACE,{"disambiguationData":[TD([makeQuery(id+"F2.opExtrude","SWEPT_FACE",FACE,{"disambiguationData":[OSD([subQ5])]})])],"derivedFrom":makeQuery(id+"F3.boolean.opBoolean","COPY",FACE,{"derivedFrom":makeQuery(id+"F3.opExtrude","CAP_FACE",FACE,{"disambiguationData":[OSD([subQ5,subQ1,subQ6,subQ7,subQ4,subQ3,subQ2,subQ0])],"isStart":false})})}),makeQuery(id+"F8.opExtrude","SWEPT_FACE",FACE,{"disambiguationData":[OSD([sQuery(id+"F7.wireOp",EDGE,"E67")])]})]});}
            var Q5;
            Q5=makeQuery(id+"F8.boolean.opBoolean","INTERSECT",EDGE,{"disambiguationData":[OD(0.0)],"derivedFrom":[makeQuery(id+"F5.opExtrude","SWEPT_FACE",FACE,{"disambiguationData":[OSD([sQuery(id+"F4.wireOp",EDGE,"E30")])]}),makeQuery(id+"F8.opExtrude","SWEPT_FACE",FACE,{"disambiguationData":[OSD([sQuery(id+"F7.wireOp",EDGE,"E67")])]})]});
            fillet(context, id + "F14", {"entities" : qUnion([Q0, Q1, Q2, Q3, Q4, Q5]), "radius" : 3 * mm, "tangentPropagation" : true, "allowEdgeOverflow" : false});
        }
        {
            var Q0;
            Q0=makeQuery(id+"F1.opExtrude","CAP_EDGE",EDGE,{"disambiguationData":[OSD([sQuery(id+"F0.wireOp",EDGE,"E1.bottom")])],"isStart":false});
            fillet(context, id + "F15", {"entities" : qUnion([Q0]), "radius" : 2 * mm, "tangentPropagation" : true, "allowEdgeOverflow" : false});
        }
        {
            var Q0;
            {var subQ0=sQuery(id+"F0.wireOp",EDGE,"E21.filletArc");var subQ1=sQuery(id+"F0.wireOp",EDGE,"E7");var subQ2=sQuery(id+"F0.wireOp",EDGE,"E6");var subQ3=sQuery(id+"F0.wireOp",EDGE,"E5");var subQ4=sQuery(id+"F0.wireOp",EDGE,"E4");var subQ5=sQuery(id+"F0.wireOp",EDGE,"E22.filletArc");var subQ6=sQuery(id+"F0.wireOp",EDGE,"E1.bottom");var subQ7=sQuery(id+"F0.wireOp",EDGE,"E1.right");var subQ8=sQuery(id+"F0.wireOp",EDGE,"E1.top");var subQ9=sQuery(id+"F0.wireOp",EDGE,"E1.left");var subQ10=sQuery(id+"F0.wireOp",EDGE,"E23.filletArc");var subQ11=sQuery(id+"F0.wireOp",EDGE,"E24.filletArc");Q0=makeQuery(id+"F2.boolean.opBoolean","SPLIT",FACE,{"disambiguationData":[TD([makeQuery(id+"F1.opExtrude","SWEPT_FACE",FACE,{"disambiguationData":[OSD([subQ6])]})])],"derivedFrom":makeQuery(id+"F1.opExtrude","CAP_FACE",FACE,{"disambiguationData":[OSD([subQ6,subQ8,subQ9,subQ7,subQ4,subQ3,subQ2,subQ1,subQ0,subQ5,subQ10,subQ11])],"isStart":true})});}
            var sketch = newSketch(context, id + "F16", { "sketchPlane" : qUnion([Q0])});
            skLineSegment(sketch, "E79.0", {"start": v(80, -80) * mm, "end": v(80, 80) * mm});
            skArc(sketch, "E79.1", {"start": v(80, 80) * mm, "mid": v(77.07, 87.07) * mm, "end": v(70, 90) * mm});
            skLineSegment(sketch, "E79.2", {"start": v(-70, 90) * mm, "end": v(70, 90) * mm});
            skCircle(sketch, "E79.3", {"center": v(60, 67.5) * mm, "radius": 4 * mm});
            skArc(sketch, "E79.4", {"start": v(-70, 90) * mm, "mid": v(-77.07, 87.07) * mm, "end": v(-80, 80) * mm});
            skLineSegment(sketch, "E79.5", {"start": v(-80, -80) * mm, "end": v(-80, 80) * mm});
            skArc(sketch, "E79.6", {"start": v(56.15, 48.18) * mm, "mid": v(0, 67.5) * mm, "end": v(-56.15, 48.18) * mm});
            skArc(sketch, "E79.7", {"start": v(60, 40.3) * mm, "mid": v(58.99, 44.68) * mm, "end": v(56.15, 48.18) * mm});
            skLineSegment(sketch, "E79.8", {"start": v(60, 40.3) * mm, "end": v(60, -40.3) * mm});
            skArc(sketch, "E79.9", {"start": v(56.15, -48.18) * mm, "mid": v(58.99, -44.68) * mm, "end": v(60, -40.3) * mm});
            skArc(sketch, "E79.10", {"start": v(-56.15, -48.18) * mm, "mid": v(0, -67.5) * mm, "end": v(56.15, -48.18) * mm});
            skLineSegment(sketch, "E79.11", {"start": v(-60, 40.3) * mm, "end": v(-60, -40.3) * mm});
            skArc(sketch, "E79.12", {"start": v(-56.15, 48.18) * mm, "mid": v(-58.99, 44.68) * mm, "end": v(-60, 40.3) * mm});
            skLineSegment(sketch, "E79.13", {"start": v(-70, -90) * mm, "end": v(70, -90) * mm});
            skArc(sketch, "E79.14", {"start": v(-80, -80) * mm, "mid": v(-77.07, -87.07) * mm, "end": v(-70, -90) * mm});
            skArc(sketch, "E79.15", {"start": v(70, -90) * mm, "mid": v(77.07, -87.07) * mm, "end": v(80, -80) * mm});
            skCircle(sketch, "E79.16", {"center": v(60, -67.5) * mm, "radius": 4 * mm});
            skCircle(sketch, "E79.17", {"center": v(-60, -67.5) * mm, "radius": 4 * mm});
            skCircle(sketch, "E79.18", {"center": v(-60, 67.5) * mm, "radius": 4 * mm});
            skArc(sketch, "E79.19", {"start": v(-60, -40.3) * mm, "mid": v(-58.99, -44.68) * mm, "end": v(-56.15, -48.18) * mm});
            skCircle(sketch, "E80", {"center": v(0, 120) * mm, "radius": 6 * mm});
            skArc(sketch, "E81", {"start": v(15, 120) * mm, "mid": v(0, 135) * mm, "end": v(-15, 120) * mm});
            skLineSegment(sketch, "E82", {"start": v(-15, 120) * mm, "end": v(-15, 108) * mm});
            skLineSegment(sketch, "E83", {"start": v(15, 120) * mm, "end": v(15, 108) * mm});
            skLineSegment(sketch, "E84", {"start": v(15, 108) * mm, "end": v(33, 90) * mm});
            skLineSegment(sketch, "E85", {"start": v(-15, 108) * mm, "end": v(-33, 90) * mm});
            skLineSegment(sketch, "E86", {"start": v(0, 120) * mm, "end": v(0, 90) * mm, "construction": true});
            skLineSegment(sketch, "E87", {"start": v(-80, 0) * mm, "end": v(80, 0) * mm, "construction": true});
            skLineSegment(sketch, "E88.MirrorCS", {"start": v(15, -108) * mm, "end": v(33, -90) * mm});
            skLineSegment(sketch, "E89.MirrorCS", {"start": v(0, -120) * mm, "end": v(0, -90) * mm, "construction": true});
            skCircle(sketch, "E90.MirrorC", {"center": v(0, -120) * mm, "radius": 6 * mm});
            skLineSegment(sketch, "E91.MirrorCS", {"start": v(15, -120) * mm, "end": v(15, -108) * mm});
            skLineSegment(sketch, "E92.MirrorCS", {"start": v(-15, -120) * mm, "end": v(-15, -108) * mm});
            skLineSegment(sketch, "E93.MirrorCS", {"start": v(-15, -108) * mm, "end": v(-33, -90) * mm});
            skArc(sketch, "E94.MirrorCS", {"start": v(15, -120) * mm, "mid": v(0, -135) * mm, "end": v(-15, -120) * mm});
            skSolve(sketch);
        }
        {
            var Q0;
            Q0=makeQuery(id+"F16.imprint","IMPRINT",FACE,{"disambiguationData":[TD([[makeQuery(id+"F16.imprint","IMPRINT",EDGE,{"derivedFrom":sQuery(id+"F16.wireOp",EDGE,"E80")}),-1.0]])]});
            var Q1;
            Q1=makeQuery(id+"F16.imprint","IMPRINT",FACE,{"disambiguationData":[TD([[makeQuery(id+"F16.imprint","IMPRINT",EDGE,{"derivedFrom":sQuery(id+"F16.wireOp",EDGE,"E79.0")}),1.0]])]});
            var Q2;
            {var subQ0=sQuery(id+"F16.wireOp",EDGE,"E88.MirrorCS");Q2=makeQuery(id+"F16.imprint","IMPRINT",FACE,{"disambiguationData":[TD([[makeQuery(id+"F16.imprint","IMPRINT",EDGE,{"derivedFrom":subQ0}),1.0]])]});}
            var Q3;
            Q3=makeQuery(id+"F2.opExtrude","CAP_FACE",FACE,{"disambiguationData":[OSD([sQuery(id+"F0.wireOp",EDGE,"E12"),sQuery(id+"F0.wireOp",EDGE,"E13"),sQuery(id+"F0.wireOp",EDGE,"E14"),sQuery(id+"F0.wireOp",EDGE,"E15"),sQuery(id+"F0.wireOp",EDGE,"E17.filletArc"),sQuery(id+"F0.wireOp",EDGE,"E18.filletArc"),sQuery(id+"F0.wireOp",EDGE,"E19.filletArc"),sQuery(id+"F0.wireOp",EDGE,"E20.filletArc"),sQuery(id+"F0.wireOp",EDGE,"E25.0"),sQuery(id+"F0.wireOp",EDGE,"E25.1"),sQuery(id+"F0.wireOp",EDGE,"E25.2"),sQuery(id+"F0.wireOp",EDGE,"E25.3"),sQuery(id+"F0.wireOp",EDGE,"E25.4"),sQuery(id+"F0.wireOp",EDGE,"E25.5"),sQuery(id+"F0.wireOp",EDGE,"E25.6"),sQuery(id+"F0.wireOp",EDGE,"E25.7")])],"isStart":false});
            extrude(context, id + "F17", {"entities" : qUnion([Q0, Q1, Q2]), "endBound" : BoundingType.UP_TO_SURFACE, "endBoundEntityFace" : qUnion([Q3]), "depth" : 25 * mm});
        }
    });
